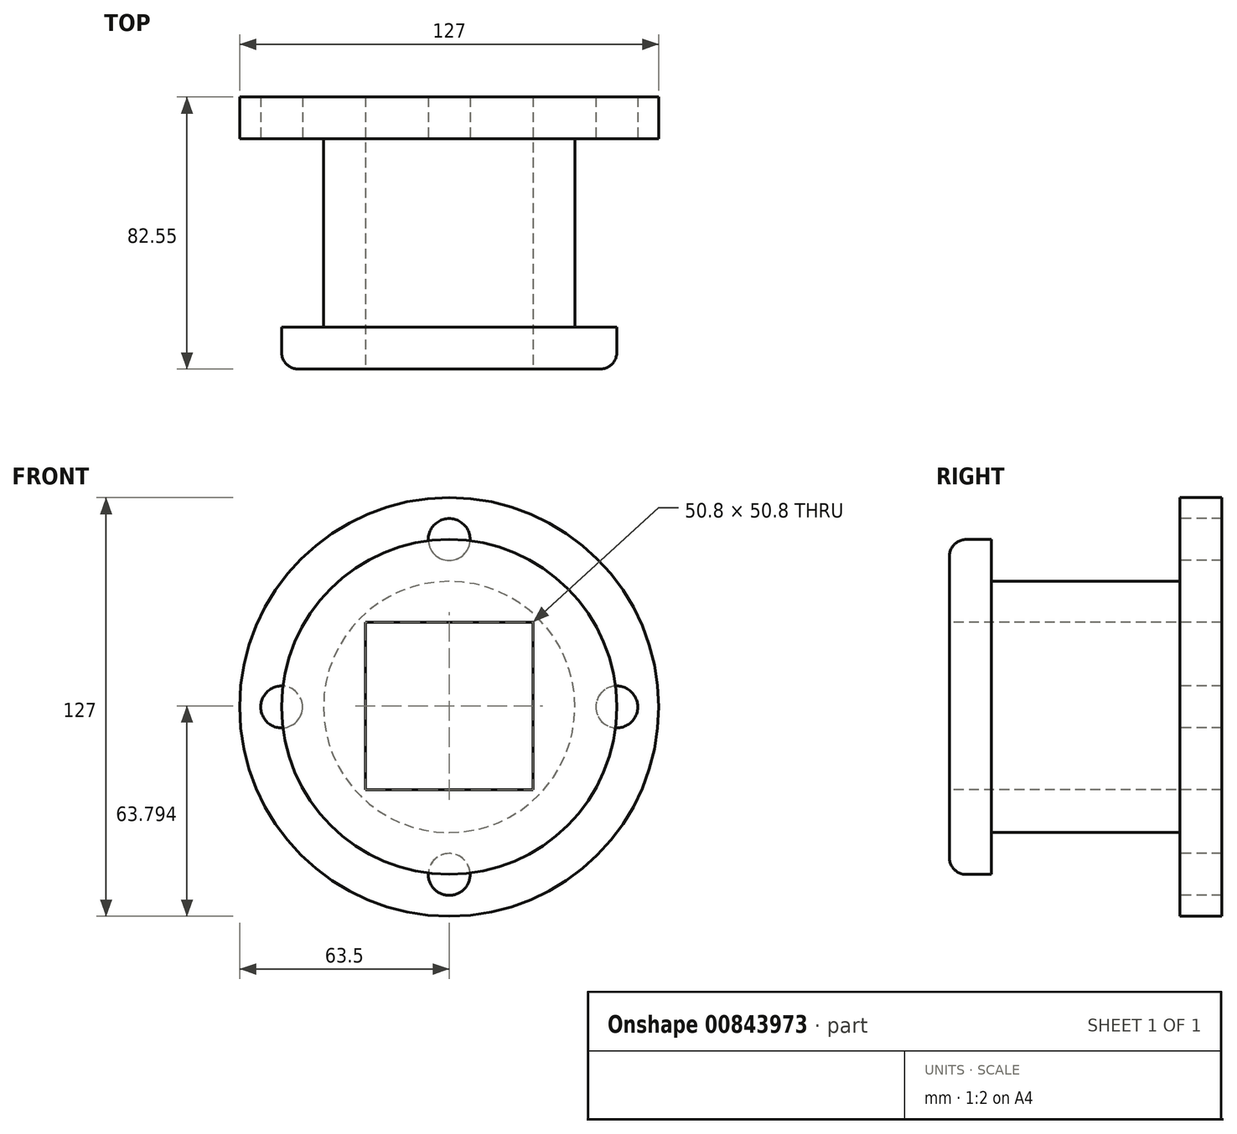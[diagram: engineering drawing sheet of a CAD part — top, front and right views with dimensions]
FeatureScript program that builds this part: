
annotation { "Feature Type Name" : "Feature", "Feature Type Description" : "" }
export const myFeature = defineFeature(function(context is Context, id is Id, definition is map)
    precondition{}
    {
        {
            var Q0;
            Q0=qCreatedBy(makeId("Front.planeOp"),FACE);
            var sketch = newSketch(context, id + "F0", { "sketchPlane" : qUnion([Q0])});
            skCircle(sketch, "E0", {"center": v(0, 0) * mm, "radius": 63.5 * mm});
            skSolve(sketch);
        }
        {
            var Q0;
            Q0 = qSketchRegion(id + "F0", true);
            var Q1;
            Q1=makeQuery(id+"F0.imprint","IMPRINT",FACE,{"disambiguationData":[TD([[makeQuery(id+"F0.imprint","IMPRINT",EDGE,{"derivedFrom":sQuery(id+"F0.wireOp",EDGE,"E0")}),1.0]])]});
            extrude(context, id + "F1", {"entities" : qUnion([Q0, Q1]), "depth" : 12.7 * mm, "offsetDistance" : 25.4 * mm});
        }
        {
            var Q0;
            Q0=makeQuery(id+"F1.opExtrude","CAP_FACE",FACE,{"disambiguationData":[OSD([sQuery(id+"F0.wireOp",EDGE,"E0")])],"isStart":false});
            var sketch = newSketch(context, id + "F2", { "sketchPlane" : qUnion([Q0])});
            skCircle(sketch, "E1", {"center": v(0, 0) * mm, "radius": 38.1 * mm});
            skSolve(sketch);
        }
        {
            var Q0;
            Q0=makeQuery(id+"F2.imprint","IMPRINT",FACE,{"disambiguationData":[TD([[makeQuery(id+"F2.imprint","IMPRINT",EDGE,{"derivedFrom":sQuery(id+"F2.wireOp",EDGE,"E1")}),1.0]])]});
            extrude(context, id + "F3", {"entities" : qUnion([Q0]), "operationType" : NewBodyOperationType.ADD, "depth" : 57.15 * mm, "offsetDistance" : 25.4 * mm});
        }
        {
            var Q0;
            Q0=makeQuery(id+"F1.opExtrude","CAP_FACE",FACE,{"disambiguationData":[OSD([sQuery(id+"F0.wireOp",EDGE,"E0")])],"isStart":false});
            var sketch = newSketch(context, id + "F4", { "sketchPlane" : qUnion([Q0])});
            skCircle(sketch, "E2", {"center": v(0, 50.8) * mm, "radius": 6.35 * mm});
            skCircle(sketch, "E3", {"center": v(50.8, 0) * mm, "radius": 6.35 * mm});
            skCircle(sketch, "E4", {"center": v(0, -50.8) * mm, "radius": 6.35 * mm});
            skCircle(sketch, "E5", {"center": v(-50.8, 0) * mm, "radius": 6.35 * mm});
            skPoint(sketch, "E6.orphan", {"position": v(-38.1, 0) * mm});
            skPoint(sketch, "E7.start.orphan", {"position": v(0, 38.1) * mm});
            skPoint(sketch, "E8.orphan", {"position": v(38.1, 0) * mm});
            skPoint(sketch, "E9.start.orphan", {"position": v(0, -38.1) * mm});
            skSolve(sketch);
        }
        {
            var Q0;
            Q0=makeQuery(id+"F4.imprint","IMPRINT",FACE,{"disambiguationData":[TD([[makeQuery(id+"F4.imprint","IMPRINT",EDGE,{"derivedFrom":sQuery(id+"F4.wireOp",EDGE,"E3")}),1.0]])]});
            var Q1;
            Q1=makeQuery(id+"F4.imprint","IMPRINT",FACE,{"disambiguationData":[TD([[makeQuery(id+"F4.imprint","IMPRINT",EDGE,{"derivedFrom":sQuery(id+"F4.wireOp",EDGE,"E4")}),1.0]])]});
            var Q2;
            Q2=makeQuery(id+"F4.imprint","IMPRINT",FACE,{"disambiguationData":[TD([[makeQuery(id+"F4.imprint","IMPRINT",EDGE,{"derivedFrom":sQuery(id+"F4.wireOp",EDGE,"E5")}),1.0]])]});
            var Q3;
            Q3=makeQuery(id+"F4.imprint","IMPRINT",FACE,{"disambiguationData":[TD([[makeQuery(id+"F4.imprint","IMPRINT",EDGE,{"derivedFrom":sQuery(id+"F4.wireOp",EDGE,"E2")}),1.0]])]});
            extrude(context, id + "F5", {"entities" : qUnion([Q0, Q1, Q2, Q3]), "operationType" : NewBodyOperationType.REMOVE, "oppositeDirection" : true, "depth" : 25.4 * mm, "offsetDistance" : 25.4 * mm});
        }
        {
            var Q0;
            Q0=makeQuery(id+"F3.opExtrude","CAP_FACE",FACE,{"disambiguationData":[OSD([sQuery(id+"F2.wireOp",EDGE,"E1")])],"isStart":false});
            var sketch = newSketch(context, id + "F6", { "sketchPlane" : qUnion([Q0])});
            skCircle(sketch, "E10", {"center": v(0, 0) * mm, "radius": 50.8 * mm});
            skSolve(sketch);
        }
        {
            var Q0;
            Q0 = qSketchRegion(id + "F6", true);
            extrude(context, id + "F7", {"entities" : qUnion([Q0]), "operationType" : NewBodyOperationType.ADD, "depth" : 12.7 * mm, "offsetDistance" : 25.4 * mm});
        }
        {
            var Q0;
            Q0=makeQuery(id+"F7.opExtrude","CAP_EDGE",EDGE,{"disambiguationData":[OSD([sQuery(id+"F6.wireOp",EDGE,"E10")])],"isStart":false});
            fillet(context, id + "F8", {"entities" : qUnion([Q0]), "radius" : 5.08 * mm, "tangentPropagation" : true, "allowEdgeOverflow" : false});
        }
        {
            var Q0;
            Q0=makeQuery(id+"F7.opExtrude","CAP_FACE",FACE,{"disambiguationData":[OSD([sQuery(id+"F6.wireOp",EDGE,"E10")])],"isStart":false});
            var sketch = newSketch(context, id + "F9", { "sketchPlane" : qUnion([Q0])});
            skLineSegment(sketch, "E11.bottom", {"start": v(-25.4, 25.7) * mm, "end": v(25.4, 25.7) * mm});
            skLineSegment(sketch, "E11.top", {"start": v(-25.4, -25.1) * mm, "end": v(25.4, -25.1) * mm});
            skLineSegment(sketch, "E11.left", {"start": v(-25.4, 25.7) * mm, "end": v(-25.4, -25.1) * mm});
            skLineSegment(sketch, "E11.right", {"start": v(25.4, 25.7) * mm, "end": v(25.4, -25.1) * mm});
            skSolve(sketch);
        }
        {
            var Q0;
            Q0=makeQuery(id+"F9.imprint","IMPRINT",FACE,{"disambiguationData":[TD([[makeQuery(id+"F9.imprint","IMPRINT",EDGE,{"derivedFrom":sQuery(id+"F9.wireOp",EDGE,"E11.bottom")}),-1.0]])]});
            extrude(context, id + "F10", {"entities" : qUnion([Q0]), "operationType" : NewBodyOperationType.REMOVE, "oppositeDirection" : true, "depth" : 127 * mm, "offsetDistance" : 25.4 * mm});
        }
    });
